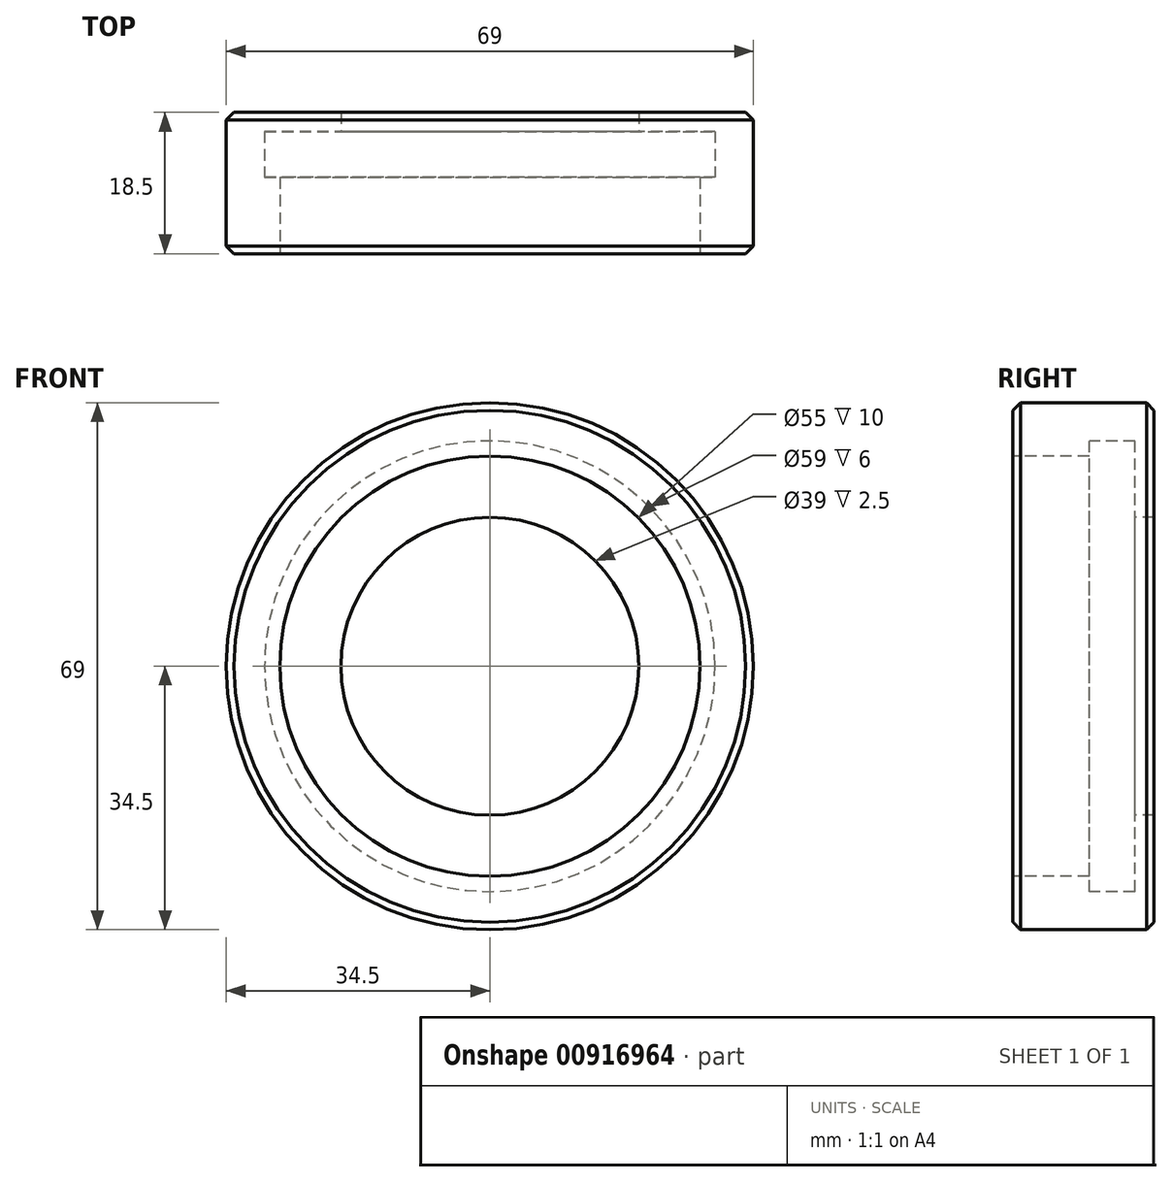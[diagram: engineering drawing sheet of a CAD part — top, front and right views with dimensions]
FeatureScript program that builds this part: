
annotation { "Feature Type Name" : "Feature", "Feature Type Description" : "" }
export const myFeature = defineFeature(function(context is Context, id is Id, definition is map)
    precondition{}
    {
        {
            var Q0;
            Q0=qCreatedBy(makeId("Front.planeOp"),FACE);
            var sketch = newSketch(context, id + "F0", { "sketchPlane" : qUnion([Q0])});
            skCircle(sketch, "E0", {"center": v(0, 0) * mm, "radius": 34.5 * mm});
            skSolve(sketch);
        }
        {
            var Q0;
            Q0=makeQuery(id+"F0.imprint","IMPRINT",FACE,{"disambiguationData":[TD([[makeQuery(id+"F0.imprint","IMPRINT",EDGE,{"derivedFrom":sQuery(id+"F0.wireOp",EDGE,"E0")}),1.0]])]});
            extrude(context, id + "F1", {"entities" : qUnion([Q0]), "depth" : 18.5 * mm, "offsetDistance" : 25 * mm});
        }
        {
            var Q0;
            Q0=makeQuery(id+"F1.opExtrude","CAP_FACE",FACE,{"disambiguationData":[OSD([sQuery(id+"F0.wireOp",EDGE,"E0")])],"isStart":false});
            var sketch = newSketch(context, id + "F2", { "sketchPlane" : qUnion([Q0])});
            skCircle(sketch, "E1", {"center": v(0, 0) * mm, "radius": 27.5 * mm});
            skSolve(sketch);
        }
        {
            var Q0;
            Q0=makeQuery(id+"F2.imprint","IMPRINT",FACE,{"disambiguationData":[TD([[makeQuery(id+"F2.imprint","IMPRINT",EDGE,{"derivedFrom":sQuery(id+"F2.wireOp",EDGE,"E1")}),1.0]])]});
            extrude(context, id + "F3", {"entities" : qUnion([Q0]), "operationType" : NewBodyOperationType.REMOVE, "oppositeDirection" : true, "depth" : 10 * mm, "offsetDistance" : 25 * mm});
        }
        {
            var Q0;
            Q0=makeQuery(id+"F3.boolean.opBoolean","COPY",FACE,{"derivedFrom":makeQuery(id+"F3.opExtrude","CAP_FACE",FACE,{"disambiguationData":[OSD([sQuery(id+"F2.wireOp",EDGE,"E1")])],"isStart":false})});
            var sketch = newSketch(context, id + "F4", { "sketchPlane" : qUnion([Q0])});
            skCircle(sketch, "E2", {"center": v(0, 0) * mm, "radius": 29.5 * mm});
            skSolve(sketch);
        }
        {
            var Q0;
            Q0 = qSketchRegion(id + "F4", true);
            extrude(context, id + "F5", {"entities" : qUnion([Q0]), "operationType" : NewBodyOperationType.REMOVE, "oppositeDirection" : true, "depth" : 6 * mm, "offsetDistance" : 25 * mm});
        }
        {
            var Q0;
            Q0=makeQuery(id+"F5.boolean.opBoolean","COPY",FACE,{"derivedFrom":makeQuery(id+"F5.opExtrude","CAP_FACE",FACE,{"disambiguationData":[OSD([sQuery(id+"F4.wireOp",EDGE,"E2")])],"isStart":false})});
            var sketch = newSketch(context, id + "F6", { "sketchPlane" : qUnion([Q0])});
            skCircle(sketch, "E3", {"center": v(0, 0) * mm, "radius": 19.5 * mm});
            skSolve(sketch);
        }
        {
            var Q0;
            Q0=makeQuery(id+"F6.imprint","IMPRINT",FACE,{"disambiguationData":[TD([[makeQuery(id+"F6.imprint","IMPRINT",EDGE,{"derivedFrom":sQuery(id+"F6.wireOp",EDGE,"E3")}),1.0]])]});
            extrude(context, id + "F7", {"entities" : qUnion([Q0]), "operationType" : NewBodyOperationType.REMOVE, "endBound" : BoundingType.THROUGH_ALL, "oppositeDirection" : true, "depth" : 25 * mm, "offsetDistance" : 25 * mm});
        }
        {
            var Q0;
            Q0=makeQuery(id+"F1.opExtrude","CAP_EDGE",EDGE,{"disambiguationData":[OSD([sQuery(id+"F0.wireOp",EDGE,"E0")])],"isStart":false});
            var Q1;
            Q1=makeQuery(id+"F3.boolean.opBoolean","COPY",EDGE,{"derivedFrom":makeQuery(id+"F3.opExtrude","CAP_EDGE",EDGE,{"disambiguationData":[OSD([sQuery(id+"F2.wireOp",EDGE,"E1")])],"isStart":true})});
            var Q2;
            Q2=makeQuery(id+"F1.opExtrude","CAP_EDGE",EDGE,{"disambiguationData":[OSD([sQuery(id+"F0.wireOp",EDGE,"E0")])],"isStart":true});
            chamfer(context, id + "F8", {"entities" : qUnion([Q0, Q1, Q2]), "width" : 1 * mm, "tangentPropagation" : true});
        }
    });
